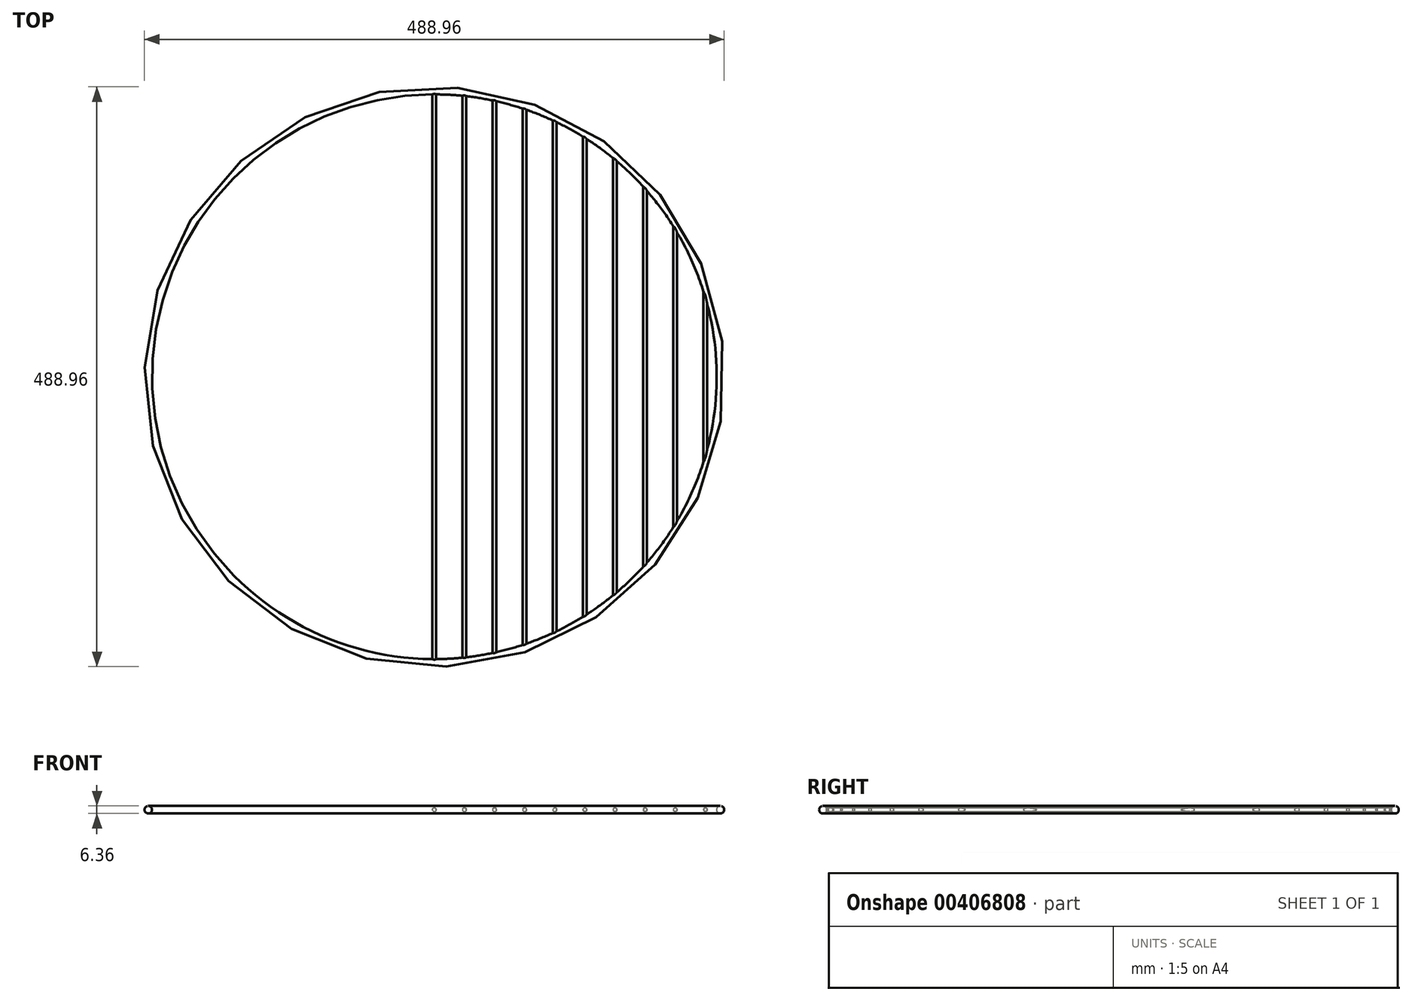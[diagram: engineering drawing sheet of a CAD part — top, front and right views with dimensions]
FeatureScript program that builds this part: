
annotation { "Feature Type Name" : "Feature", "Feature Type Description" : "" }
export const myFeature = defineFeature(function(context is Context, id is Id, definition is map)
    precondition{}
    {
        {
            var Q0;
            Q0=qCreatedBy(makeId("Front.planeOp"),FACE);
            var sketch = newSketch(context, id + "F0", { "sketchPlane" : qUnion([Q0])});
            skCircle(sketch, "E0", {"center": v(241.3, 0) * mm, "radius": 3.18 * mm});
            skLineSegment(sketch, "E1", {"start": v(0, 0) * mm, "end": v(0, 32.12) * mm, "construction": true});
            skSolve(sketch);
        }
        {
            var Q0;
            Q0=qCreatedBy(makeId("Front.planeOp"),FACE);
            var sketch = newSketch(context, id + "F1", { "sketchPlane" : qUnion([Q0])});
            skCircle(sketch, "E2", {"center": v(0, 0) * mm, "radius": 1.59 * mm});
            skCircle(sketch, "E3.1.0.0", {"center": v(25.4, 0) * mm, "radius": 1.59 * mm});
            skCircle(sketch, "E3.2.0.0", {"center": v(50.8, 0) * mm, "radius": 1.59 * mm});
            skCircle(sketch, "E3.3.0.0", {"center": v(76.2, 0) * mm, "radius": 1.59 * mm});
            skCircle(sketch, "E3.4.0.0", {"center": v(101.6, 0) * mm, "radius": 1.59 * mm});
            skCircle(sketch, "E3.5.0.0", {"center": v(127, 0) * mm, "radius": 1.59 * mm});
            skCircle(sketch, "E3.6.0.0", {"center": v(152.4, 0) * mm, "radius": 1.59 * mm});
            skCircle(sketch, "E3.7.0.0", {"center": v(177.8, 0) * mm, "radius": 1.59 * mm});
            skCircle(sketch, "E3.8.0.0", {"center": v(203.2, 0) * mm, "radius": 1.59 * mm});
            skCircle(sketch, "E3.9.0.0", {"center": v(228.6, 0) * mm, "radius": 1.59 * mm});
            skLineSegment(sketch, "E3.direction1", {"start": v(0, 0) * mm, "end": v(25.4, 0) * mm, "construction": true});
            skCircle(sketch, "E4.MirrorC", {"center": v(-25.4, 0) * mm, "radius": 1.59 * mm});
            skCircle(sketch, "E5.MirrorC", {"center": v(-50.8, 0) * mm, "radius": 1.59 * mm});
            skCircle(sketch, "E6.MirrorC", {"center": v(-101.6, 0) * mm, "radius": 1.59 * mm});
            skCircle(sketch, "E7.MirrorC", {"center": v(-127, 0) * mm, "radius": 1.59 * mm});
            skCircle(sketch, "E8.MirrorC", {"center": v(-152.4, 0) * mm, "radius": 1.59 * mm});
            skCircle(sketch, "E9.MirrorC", {"center": v(-177.8, 0) * mm, "radius": 1.59 * mm});
            skCircle(sketch, "E10.MirrorC", {"center": v(-228.6, 0) * mm, "radius": 1.59 * mm});
            skCircle(sketch, "E11.MirrorC", {"center": v(-76.2, 0) * mm, "radius": 1.59 * mm});
            skCircle(sketch, "E12.MirrorC", {"center": v(-203.2, 0) * mm, "radius": 1.59 * mm});
            skSolve(sketch);
        }
        {
            var Q0;
            Q0=makeQuery(id+"F0.imprint","IMPRINT",FACE,{"disambiguationData":[TD([[makeQuery(id+"F0.imprint","IMPRINT",EDGE,{"derivedFrom":sQuery(id+"F0.wireOp",EDGE,"E0")}),1.0]])]});
            var Q1;
            Q1=sQuery(id+"F0.wireOp",EDGE,"E1");
            revolve(context, id + "F2", {"entities" : qUnion([Q0]), "axis" : qUnion([Q1]), "revolveType" : RevolveType.FULL});
        }
        {
            var Q0;
            Q0=makeQuery(id+"F1.imprint","IMPRINT",FACE,{"disambiguationData":[TD([[makeQuery(id+"F1.imprint","IMPRINT",EDGE,{"derivedFrom":sQuery(id+"F1.wireOp",EDGE,"E2")}),1.0]])]});
            var Q1;
            Q1=makeQuery(id+"F1.imprint","IMPRINT",FACE,{"disambiguationData":[TD([[makeQuery(id+"F1.imprint","IMPRINT",EDGE,{"derivedFrom":sQuery(id+"F1.wireOp",EDGE,"E3.1.0.0")}),1.0]])]});
            var Q2;
            Q2=makeQuery(id+"F1.imprint","IMPRINT",FACE,{"disambiguationData":[TD([[makeQuery(id+"F1.imprint","IMPRINT",EDGE,{"derivedFrom":sQuery(id+"F1.wireOp",EDGE,"E3.2.0.0")}),1.0]])]});
            var Q3;
            Q3=makeQuery(id+"F1.imprint","IMPRINT",FACE,{"disambiguationData":[TD([[makeQuery(id+"F1.imprint","IMPRINT",EDGE,{"derivedFrom":sQuery(id+"F1.wireOp",EDGE,"E3.3.0.0")}),1.0]])]});
            var Q4;
            Q4=makeQuery(id+"F1.imprint","IMPRINT",FACE,{"disambiguationData":[TD([[makeQuery(id+"F1.imprint","IMPRINT",EDGE,{"derivedFrom":sQuery(id+"F1.wireOp",EDGE,"E3.4.0.0")}),1.0]])]});
            var Q5;
            Q5=makeQuery(id+"F1.imprint","IMPRINT",FACE,{"disambiguationData":[TD([[makeQuery(id+"F1.imprint","IMPRINT",EDGE,{"derivedFrom":sQuery(id+"F1.wireOp",EDGE,"E3.5.0.0")}),1.0]])]});
            var Q6;
            Q6=makeQuery(id+"F1.imprint","IMPRINT",FACE,{"disambiguationData":[TD([[makeQuery(id+"F1.imprint","IMPRINT",EDGE,{"derivedFrom":sQuery(id+"F1.wireOp",EDGE,"E3.6.0.0")}),1.0]])]});
            var Q7;
            Q7=makeQuery(id+"F1.imprint","IMPRINT",FACE,{"disambiguationData":[TD([[makeQuery(id+"F1.imprint","IMPRINT",EDGE,{"derivedFrom":sQuery(id+"F1.wireOp",EDGE,"E3.7.0.0")}),1.0]])]});
            var Q8;
            Q8=makeQuery(id+"F1.imprint","IMPRINT",FACE,{"disambiguationData":[TD([[makeQuery(id+"F1.imprint","IMPRINT",EDGE,{"derivedFrom":sQuery(id+"F1.wireOp",EDGE,"E3.8.0.0")}),1.0]])]});
            var Q9;
            Q9=makeQuery(id+"F1.imprint","IMPRINT",FACE,{"disambiguationData":[TD([[makeQuery(id+"F1.imprint","IMPRINT",EDGE,{"derivedFrom":sQuery(id+"F1.wireOp",EDGE,"E3.9.0.0")}),1.0]])]});
            var Q10;
            Q10=makeQuery(id+"F1.imprint","IMPRINT",FACE,{"disambiguationData":[TD([[makeQuery(id+"F1.imprint","IMPRINT",EDGE,{"derivedFrom":sQuery(id+"F1.wireOp",EDGE,"E4.MirrorC")}),-1.0]])]});
            var Q11;
            Q11=makeQuery(id+"F1.imprint","IMPRINT",FACE,{"disambiguationData":[TD([[makeQuery(id+"F1.imprint","IMPRINT",EDGE,{"derivedFrom":sQuery(id+"F1.wireOp",EDGE,"E5.MirrorC")}),-1.0]])]});
            var Q12;
            Q12=makeQuery(id+"F1.imprint","IMPRINT",FACE,{"disambiguationData":[TD([[makeQuery(id+"F1.imprint","IMPRINT",EDGE,{"derivedFrom":sQuery(id+"F1.wireOp",EDGE,"E11.MirrorC")}),-1.0]])]});
            var Q13;
            Q13=makeQuery(id+"F1.imprint","IMPRINT",FACE,{"disambiguationData":[TD([[makeQuery(id+"F1.imprint","IMPRINT",EDGE,{"derivedFrom":sQuery(id+"F1.wireOp",EDGE,"E6.MirrorC")}),-1.0]])]});
            var Q14;
            Q14=makeQuery(id+"F1.imprint","IMPRINT",FACE,{"disambiguationData":[TD([[makeQuery(id+"F1.imprint","IMPRINT",EDGE,{"derivedFrom":sQuery(id+"F1.wireOp",EDGE,"E7.MirrorC")}),-1.0]])]});
            var Q15;
            Q15=makeQuery(id+"F1.imprint","IMPRINT",FACE,{"disambiguationData":[TD([[makeQuery(id+"F1.imprint","IMPRINT",EDGE,{"derivedFrom":sQuery(id+"F1.wireOp",EDGE,"E8.MirrorC")}),-1.0]])]});
            var Q16;
            Q16=makeQuery(id+"F1.imprint","IMPRINT",FACE,{"disambiguationData":[TD([[makeQuery(id+"F1.imprint","IMPRINT",EDGE,{"derivedFrom":sQuery(id+"F1.wireOp",EDGE,"E12.MirrorC")}),-1.0]])]});
            var Q17;
            Q17=makeQuery(id+"F1.imprint","IMPRINT",FACE,{"disambiguationData":[TD([[makeQuery(id+"F1.imprint","IMPRINT",EDGE,{"derivedFrom":sQuery(id+"F1.wireOp",EDGE,"E10.MirrorC")}),-1.0]])]});
            var Q18;
            Q18=makeQuery(id+"F1.imprint","IMPRINT",FACE,{"disambiguationData":[TD([[makeQuery(id+"F1.imprint","IMPRINT",EDGE,{"derivedFrom":sQuery(id+"F1.wireOp",EDGE,"E9.MirrorC")}),-1.0]])]});
            extrude(context, id + "F3", {"entities" : qUnion([Q0, Q1, Q2, Q3, Q4, Q5, Q6, Q7, Q8, Q9, Q10, Q11, Q12, Q13, Q14, Q15, Q16, Q17, Q18]), "operationType" : NewBodyOperationType.ADD, "endBound" : BoundingType.UP_TO_NEXT, "depth" : 25.4 * mm, "hasSecondDirection" : true, "secondDirectionBound" : SecondDirectionBoundingType.UP_TO_NEXT, "secondDirectionOppositeDirection" : true, "secondDirectionDepth" : 25.4 * mm});
        }
    });
